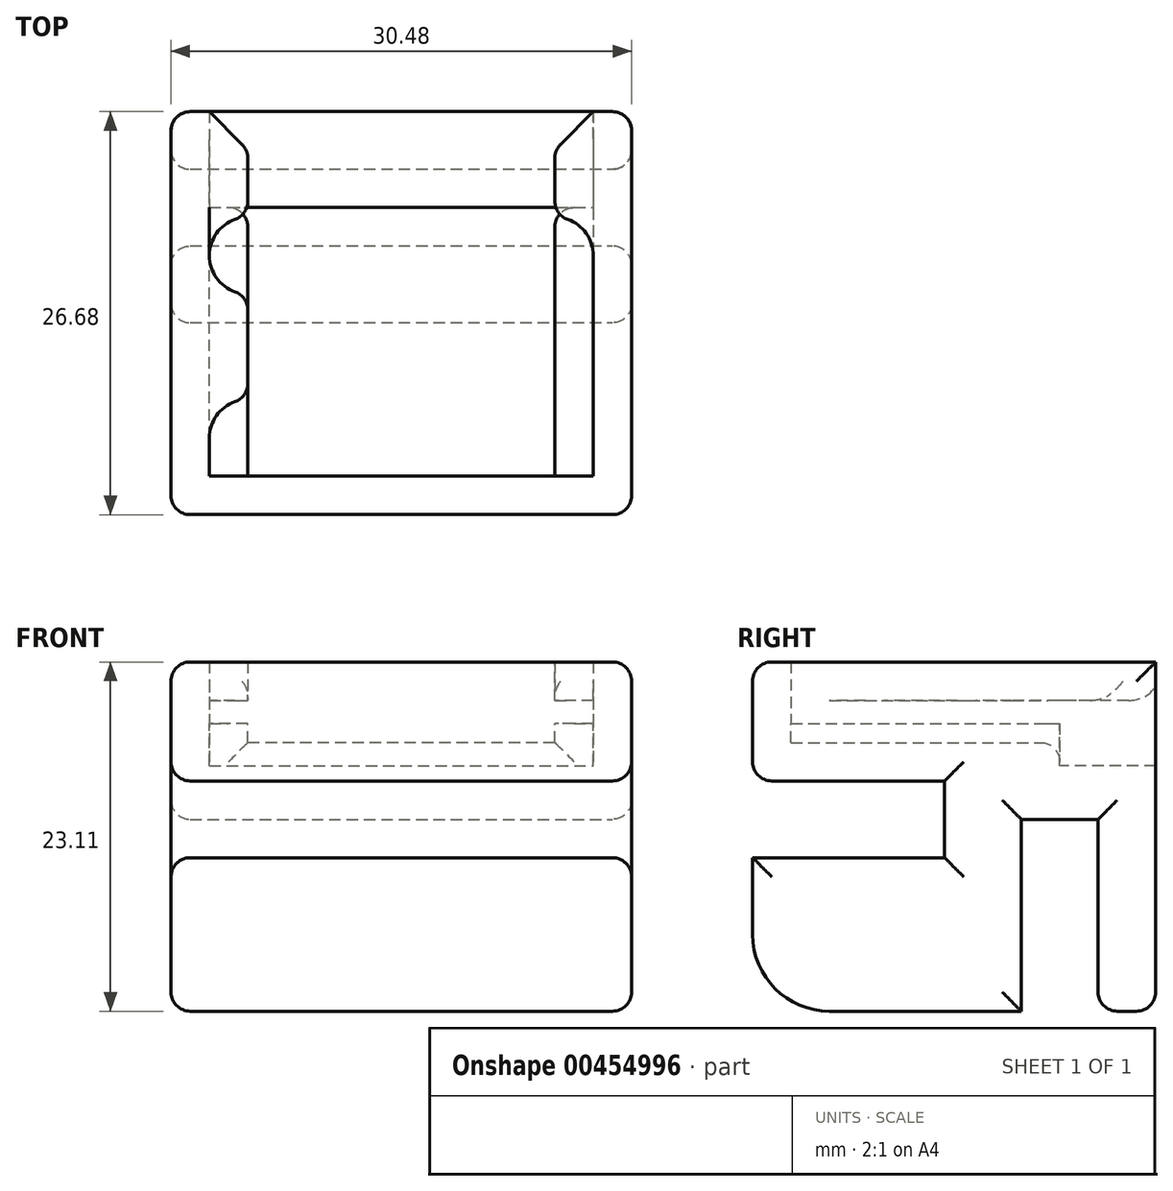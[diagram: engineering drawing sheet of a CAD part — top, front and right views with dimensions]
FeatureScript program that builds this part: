
annotation { "Feature Type Name" : "Feature", "Feature Type Description" : "" }
export const myFeature = defineFeature(function(context is Context, id is Id, definition is map)
    precondition{}
    {
        {
            var Q0;
            Q0=qCreatedBy(makeId("Top.planeOp"),FACE);
            var sketch = newSketch(context, id + "F0", { "sketchPlane" : qUnion([Q0])});
            skLineSegment(sketch, "E0.bottom", {"start": v(15.24, 13.33) * mm, "end": v(-15.24, 13.33) * mm});
            skLineSegment(sketch, "E0.top", {"start": v(15.24, -13.34) * mm, "end": v(-15.24, -13.34) * mm});
            skLineSegment(sketch, "E0.left", {"start": v(15.24, 13.33) * mm, "end": v(15.24, -13.34) * mm});
            skLineSegment(sketch, "E0.right", {"start": v(-15.24, 13.34) * mm, "end": v(-15.24, -13.33) * mm});
            skPoint(sketch, "E0.middle", {"position": v(0, 0) * mm});
            skSolve(sketch);
        }
        {
            var Q0;
            Q0 = qSketchRegion(id + "F0", true);
            extrude(context, id + "F1", {"entities" : qUnion([Q0]), "depth" : 19.05 * mm});
        }
        {
            var Q0;
            Q0=makeQuery(id+"F1.opExtrude","CAP_FACE",FACE,{"disambiguationData":[OSD([sQuery(id+"F0.wireOp",EDGE,"E0.bottom"),sQuery(id+"F0.wireOp",EDGE,"E0.top"),sQuery(id+"F0.wireOp",EDGE,"E0.left"),sQuery(id+"F0.wireOp",EDGE,"E0.right")])],"isStart":false});
            var sketch = newSketch(context, id + "F2", { "sketchPlane" : qUnion([Q0])});
            skLineSegment(sketch, "E1", {"start": v(-15.24, 13.33) * mm, "end": v(-15.24, -13.33) * mm});
            skLineSegment(sketch, "E2", {"start": v(-15.24, -13.33) * mm, "end": v(15.24, -13.34) * mm});
            skLineSegment(sketch, "E3", {"start": v(15.24, -13.34) * mm, "end": v(15.24, 13.33) * mm});
            skLineSegment(sketch, "E4", {"start": v(15.24, 13.33) * mm, "end": v(12.7, 13.33) * mm});
            skLineSegment(sketch, "E5", {"start": v(12.7, 13.33) * mm, "end": v(12.7, -10.8) * mm});
            skLineSegment(sketch, "E6", {"start": v(12.7, -10.8) * mm, "end": v(-12.7, -10.8) * mm});
            skLineSegment(sketch, "E7", {"start": v(-12.7, -10.8) * mm, "end": v(-12.7, 13.33) * mm});
            skLineSegment(sketch, "E8", {"start": v(-12.7, 13.33) * mm, "end": v(-15.24, 13.33) * mm});
            skLineSegment(sketch, "E9", {"start": v(-12.7, -10.8) * mm, "end": v(-12.7, -13.34) * mm, "construction": true});
            skSolve(sketch);
        }
        {
            var Q0;
            Q0 = qSketchRegion(id + "F2", true);
            extrude(context, id + "F3", {"entities" : qUnion([Q0]), "operationType" : NewBodyOperationType.ADD, "depth" : 1.52 * mm});
        }
        {
            var Q0;
            Q0=makeQuery(id+"F3.opExtrude","CAP_FACE",FACE,{"disambiguationData":[OSD([sQuery(id+"F2.wireOp",EDGE,"E1"),sQuery(id+"F2.wireOp",EDGE,"E2"),sQuery(id+"F2.wireOp",EDGE,"E3"),sQuery(id+"F2.wireOp",EDGE,"E4"),sQuery(id+"F2.wireOp",EDGE,"E5"),sQuery(id+"F2.wireOp",EDGE,"E6"),sQuery(id+"F2.wireOp",EDGE,"E7"),sQuery(id+"F2.wireOp",EDGE,"E8")])],"isStart":false});
            var sketch = newSketch(context, id + "F4", { "sketchPlane" : qUnion([Q0])});
            skLineSegment(sketch, "E10.0", {"start": v(15.24, 13.33) * mm, "end": v(12.7, 13.33) * mm});
            skLineSegment(sketch, "E10.1", {"start": v(15.24, 13.33) * mm, "end": v(15.24, -13.34) * mm});
            skLineSegment(sketch, "E10.2", {"start": v(15.24, -13.34) * mm, "end": v(-15.24, -13.34) * mm});
            skLineSegment(sketch, "E10.3", {"start": v(-15.24, 13.33) * mm, "end": v(-15.24, -13.33) * mm});
            skLineSegment(sketch, "E11.0", {"start": v(-12.7, 13.33) * mm, "end": v(-15.24, 13.33) * mm});
            skLineSegment(sketch, "E12", {"start": v(-12.7, 13.33) * mm, "end": v(-10.16, 10.8) * mm});
            skLineSegment(sketch, "E13", {"start": v(-10.16, 10.8) * mm, "end": v(-10.16, -5.71) * mm});
            skLineSegment(sketch, "E14", {"start": v(-12.7, -10.8) * mm, "end": v(0, -10.8) * mm});
            skLineSegment(sketch, "E15", {"start": v(0, -10.8) * mm, "end": v(0, 0) * mm, "construction": true});
            skArc(sketch, "E16", {"start": v(-10.16, -5.71) * mm, "mid": v(-11.96, -6.46) * mm, "end": v(-12.7, -8.25) * mm});
            skLineSegment(sketch, "E17", {"start": v(-10.16, -5.71) * mm, "end": v(-10.16, -8.25) * mm, "construction": true});
            skLineSegment(sketch, "E18", {"start": v(-12.7, -10.8) * mm, "end": v(-12.7, -8.25) * mm});
            skArc(sketch, "E19", {"start": v(-10.16, 6.35) * mm, "mid": v(-12.7, 3.81) * mm, "end": v(-10.16, 1.27) * mm});
            skLineSegment(sketch, "E20.MirrorCS", {"start": v(12.7, -10.8) * mm, "end": v(0, -10.8) * mm});
            skLineSegment(sketch, "E21.MirrorCS", {"start": v(10.16, -5.71) * mm, "end": v(10.16, -8.25) * mm, "construction": true});
            skArc(sketch, "E22.MirrorCS", {"start": v(10.16, -5.71) * mm, "mid": v(11.96, -6.46) * mm, "end": v(12.7, -8.25) * mm});
            skLineSegment(sketch, "E23.MirrorCS", {"start": v(12.7, 13.34) * mm, "end": v(10.16, 10.8) * mm});
            skLineSegment(sketch, "E24.MirrorCS", {"start": v(12.7, -10.8) * mm, "end": v(12.7, -8.25) * mm});
            skArc(sketch, "E25.MirrorCS", {"start": v(10.16, 6.35) * mm, "mid": v(12.7, 3.81) * mm, "end": v(10.16, 1.27) * mm});
            skLineSegment(sketch, "E26.MirrorCS", {"start": v(10.16, 10.8) * mm, "end": v(10.16, -5.71) * mm});
            skSolve(sketch);
        }
        {
            var Q0;
            {var subQ0=sQuery(id+"F4.wireOp",EDGE,"E16");Q0=makeQuery(id+"F4.imprint","IMPRINT",FACE,{"disambiguationData":[TD([[makeQuery(id+"F4.imprint","IMPRINT",EDGE,{"derivedFrom":subQ0}),-1.0]])]});}
            var Q1;
            {var subQ0=sQuery(id+"F4.wireOp",EDGE,"E12");Q1=makeQuery(id+"F4.imprint","IMPRINT",FACE,{"disambiguationData":[TD([[makeQuery(id+"F4.imprint","IMPRINT",EDGE,{"derivedFrom":subQ0}),-1.0]])]});}
            var Q2;
            {var subQ3=sQuery(id+"F4.wireOp",EDGE,"E10.0");Q2=makeQuery(id+"F4.imprint","IMPRINT",FACE,{"disambiguationData":[TD([[makeQuery(id+"F4.imprint","IMPRINT",EDGE,{"derivedFrom":subQ3}),1.0]])]});}
            var Q3;
            {var subQ0=sQuery(id+"F4.wireOp",EDGE,"E22.MirrorCS");Q3=makeQuery(id+"F4.imprint","IMPRINT",FACE,{"disambiguationData":[TD([[makeQuery(id+"F4.imprint","IMPRINT",EDGE,{"derivedFrom":subQ0}),1.0]])]});}
            var Q4;
            {var subQ0=sQuery(id+"F4.wireOp",EDGE,"E23.MirrorCS");Q4=makeQuery(id+"F4.imprint","IMPRINT",FACE,{"disambiguationData":[TD([[makeQuery(id+"F4.imprint","IMPRINT",EDGE,{"derivedFrom":subQ0}),1.0]])]});}
            extrude(context, id + "F5", {"entities" : qUnion([Q0, Q1, Q2, Q3, Q4]), "operationType" : NewBodyOperationType.ADD, "depth" : 2.54 * mm});
        }
        {
            var Q0;
            Q0=makeQuery(id+"F1.opExtrude","CAP_FACE",FACE,{"disambiguationData":[OSD([sQuery(id+"F0.wireOp",EDGE,"E0.bottom"),sQuery(id+"F0.wireOp",EDGE,"E0.top"),sQuery(id+"F0.wireOp",EDGE,"E0.left"),sQuery(id+"F0.wireOp",EDGE,"E0.right")])],"isStart":false});
            var sketch = newSketch(context, id + "F6", { "sketchPlane" : qUnion([Q0])});
            skLineSegment(sketch, "E27.bottom", {"start": v(-10.16, -10.8) * mm, "end": v(10.16, -10.8) * mm});
            skLineSegment(sketch, "E27.top", {"start": v(-10.16, 13.33) * mm, "end": v(10.16, 13.33) * mm});
            skLineSegment(sketch, "E27.left", {"start": v(-10.16, -10.8) * mm, "end": v(-10.16, 13.33) * mm});
            skLineSegment(sketch, "E27.right", {"start": v(10.16, -10.8) * mm, "end": v(10.16, 13.33) * mm});
            skPoint(sketch, "E27.middle", {"position": v(0, 1.27) * mm});
            skSolve(sketch);
        }
        {
            var Q0;
            Q0 = qSketchRegion(id + "F6", true);
            extrude(context, id + "F7", {"entities" : qUnion([Q0]), "operationType" : NewBodyOperationType.REMOVE, "oppositeDirection" : true, "depth" : 1.27 * mm});
        }
        {
            var Q0;
            {var subQ0=sQuery(id+"F0.wireOp",EDGE,"E0.bottom");Q0=makeQuery(id+"F7.boolean.opBoolean","SPLIT",FACE,{"disambiguationData":[TD([makeQuery(id+"F3.opExtrude","SWEPT_FACE",FACE,{"disambiguationData":[OSD([sQuery(id+"F2.wireOp",EDGE,"E5")])]})])],"derivedFrom":makeQuery(id+"F1.opExtrude","CAP_FACE",FACE,{"disambiguationData":[OSD([subQ0,sQuery(id+"F0.wireOp",EDGE,"E0.top"),sQuery(id+"F0.wireOp",EDGE,"E0.left"),sQuery(id+"F0.wireOp",EDGE,"E0.right")])],"isStart":false})});}
            var sketch = newSketch(context, id + "F8", { "sketchPlane" : qUnion([Q0])});
            skLineSegment(sketch, "E28.bottom", {"start": v(-12.7, 13.33) * mm, "end": v(12.7, 13.33) * mm});
            skLineSegment(sketch, "E28.top", {"start": v(-12.7, 6.98) * mm, "end": v(12.7, 6.98) * mm});
            skLineSegment(sketch, "E28.left", {"start": v(-12.7, 13.33) * mm, "end": v(-12.7, 6.98) * mm});
            skLineSegment(sketch, "E28.right", {"start": v(12.7, 13.33) * mm, "end": v(12.7, 6.98) * mm});
            skSolve(sketch);
        }
        {
            var Q0;
            Q0 = qSketchRegion(id + "F8", true);
            extrude(context, id + "F9", {"entities" : qUnion([Q0]), "operationType" : NewBodyOperationType.REMOVE, "oppositeDirection" : true, "depth" : 2.8 * mm});
        }
        {
            var Q0;
            Q0=makeQuery(id+"F5.boolean.opBoolean","MERGE",FACE,{"derivedFrom":[makeQuery(id+"F3.boolean.opBoolean","MERGE",FACE,{"derivedFrom":[makeQuery(id+"F1.opExtrude","SWEPT_FACE",FACE,{"disambiguationData":[OSD([sQuery(id+"F0.wireOp",EDGE,"E0.left")])]}),makeQuery(id+"F3.opExtrude","SWEPT_FACE",FACE,{"disambiguationData":[OSD([sQuery(id+"F2.wireOp",EDGE,"E3")])]})]}),makeQuery(id+"F5.opExtrude","SWEPT_FACE",FACE,{"disambiguationData":[OSD([sQuery(id+"F4.wireOp",EDGE,"E10.1")])]})]});
            var sketch = newSketch(context, id + "F10", { "sketchPlane" : qUnion([Q0])});
            skLineSegment(sketch, "E29.bottom", {"start": v(-13.34, 15.24) * mm, "end": v(-0.64, 15.24) * mm});
            skLineSegment(sketch, "E29.top", {"start": v(-13.34, 10.16) * mm, "end": v(-0.64, 10.16) * mm});
            skLineSegment(sketch, "E29.left", {"start": v(-13.34, 15.24) * mm, "end": v(-13.34, 10.16) * mm});
            skLineSegment(sketch, "E29.right", {"start": v(-0.64, 15.24) * mm, "end": v(-0.63, 10.16) * mm});
            skLineSegment(sketch, "E30.bottom", {"start": v(4.44, 0) * mm, "end": v(9.52, 0) * mm});
            skLineSegment(sketch, "E30.top", {"start": v(4.44, 12.7) * mm, "end": v(9.52, 12.7) * mm});
            skLineSegment(sketch, "E30.left", {"start": v(4.44, 0) * mm, "end": v(4.44, 12.7) * mm});
            skLineSegment(sketch, "E30.right", {"start": v(9.53, 0) * mm, "end": v(9.53, 12.7) * mm});
            skSolve(sketch);
        }
        {
            var Q0;
            Q0 = qSketchRegion(id + "F10", true);
            extrude(context, id + "F11", {"entities" : qUnion([Q0]), "operationType" : NewBodyOperationType.REMOVE, "endBound" : BoundingType.THROUGH_ALL, "oppositeDirection" : true, "depth" : 25.4 * mm});
        }
        {
            var Q0;
            Q0=makeQuery(id+"F1.opExtrude","CAP_EDGE",EDGE,{"disambiguationData":[OSD([sQuery(id+"F0.wireOp",EDGE,"E0.top")])],"isStart":true});
            fillet(context, id + "F12", {"entities" : qUnion([Q0]), "radius" : 5.08 * mm, "tangentPropagation" : true, "allowEdgeOverflow" : false});
        }
        {
            var Q0;
            Q0=makeQuery(id+"F11.boolean.opBoolean","COPY",EDGE,{"derivedFrom":makeQuery(id+"F11.opExtrude","SWEPT_EDGE",EDGE,{"disambiguationData":[OSD([sQuery(id+"F0.wireOp",EDGE,"E0.top"),sQuery(id+"F0.wireOp",EDGE,"E0.left"),sQuery(id+"F2.wireOp",EDGE,"E2"),sQuery(id+"F2.wireOp",EDGE,"E3"),sQuery(id+"F4.wireOp",EDGE,"E10.1"),sQuery(id+"F4.wireOp",EDGE,"E10.2"),sQuery(id+"F10.wireOp",EDGE,"E29.top"),sQuery(id+"F10.wireOp",EDGE,"E29.left")])]})});
            var Q1;
            Q1=makeQuery(id+"F11.boolean.opBoolean","COPY",EDGE,{"derivedFrom":makeQuery(id+"F11.opExtrude","SWEPT_EDGE",EDGE,{"disambiguationData":[OSD([sQuery(id+"F0.wireOp",EDGE,"E0.top"),sQuery(id+"F0.wireOp",EDGE,"E0.left"),sQuery(id+"F2.wireOp",EDGE,"E2"),sQuery(id+"F2.wireOp",EDGE,"E3"),sQuery(id+"F4.wireOp",EDGE,"E10.1"),sQuery(id+"F4.wireOp",EDGE,"E10.2"),sQuery(id+"F10.wireOp",EDGE,"E29.bottom"),sQuery(id+"F10.wireOp",EDGE,"E29.left")])]})});
            var Q2;
            Q2=makeQuery(id+"F11.boolean.opBoolean","COPY",EDGE,{"derivedFrom":makeQuery(id+"F11.opExtrude","SWEPT_EDGE",EDGE,{"disambiguationData":[OSD([sQuery(id+"F0.wireOp",EDGE,"E0.left"),sQuery(id+"F10.wireOp",EDGE,"E30.bottom"),sQuery(id+"F10.wireOp",EDGE,"E30.left")])]})});
            var Q3;
            Q3=makeQuery(id+"F11.boolean.opBoolean","COPY",EDGE,{"derivedFrom":makeQuery(id+"F11.opExtrude","SWEPT_EDGE",EDGE,{"disambiguationData":[OSD([sQuery(id+"F0.wireOp",EDGE,"E0.left"),sQuery(id+"F10.wireOp",EDGE,"E30.bottom"),sQuery(id+"F10.wireOp",EDGE,"E30.right")])]})});
            var Q4;
            Q4=makeQuery(id+"F5.boolean.opBoolean","MERGE",FACE,{"derivedFrom":[makeQuery(id+"F3.boolean.opBoolean","MERGE",FACE,{"derivedFrom":[makeQuery(id+"F1.opExtrude","SWEPT_FACE",FACE,{"disambiguationData":[OSD([sQuery(id+"F0.wireOp",EDGE,"E0.left")])]}),makeQuery(id+"F3.opExtrude","SWEPT_FACE",FACE,{"disambiguationData":[OSD([sQuery(id+"F2.wireOp",EDGE,"E3")])]})]}),makeQuery(id+"F5.opExtrude","SWEPT_FACE",FACE,{"disambiguationData":[OSD([sQuery(id+"F4.wireOp",EDGE,"E10.1")])]})]});
            var Q5;
            Q5=makeQuery(id+"F5.boolean.opBoolean","MERGE",FACE,{"derivedFrom":[makeQuery(id+"F3.boolean.opBoolean","MERGE",FACE,{"derivedFrom":[makeQuery(id+"F1.opExtrude","SWEPT_FACE",FACE,{"disambiguationData":[OSD([sQuery(id+"F0.wireOp",EDGE,"E0.right")])]}),makeQuery(id+"F3.opExtrude","SWEPT_FACE",FACE,{"disambiguationData":[OSD([sQuery(id+"F2.wireOp",EDGE,"E1")])]})]}),makeQuery(id+"F5.opExtrude","SWEPT_FACE",FACE,{"disambiguationData":[OSD([sQuery(id+"F4.wireOp",EDGE,"E10.3")])]})]});
            var Q6;
            Q6=makeQuery(id+"F9.boolean.opBoolean","COPY",EDGE,{"derivedFrom":makeQuery(id+"F9.opExtrude","CAP_EDGE",EDGE,{"disambiguationData":[OSD([sQuery(id+"F8.wireOp",EDGE,"E28.bottom")])],"isStart":false})});
            var Q7;
            Q7=makeQuery(id+"F9.boolean.opBoolean","INTERSECT",EDGE,{"derivedFrom":[makeQuery(id+"F7.boolean.opBoolean","COPY",FACE,{"derivedFrom":makeQuery(id+"F7.opExtrude","CAP_FACE",FACE,{"disambiguationData":[OSD([sQuery(id+"F6.wireOp",EDGE,"E27.bottom"),sQuery(id+"F6.wireOp",EDGE,"E27.top"),sQuery(id+"F6.wireOp",EDGE,"E27.left"),sQuery(id+"F6.wireOp",EDGE,"E27.right")])],"isStart":false})}),makeQuery(id+"F9.opExtrude","SWEPT_FACE",FACE,{"disambiguationData":[OSD([sQuery(id+"F8.wireOp",EDGE,"E28.top")])]})]});
            var Q8;
            {var subQ0=sQuery(id+"F8.wireOp",EDGE,"E28.top");Q8=makeQuery(id+"F9.boolean.opBoolean","COPY",EDGE,{"disambiguationData":[TD([makeQuery(id+"F3.opExtrude","SWEPT_FACE",FACE,{"disambiguationData":[OSD([sQuery(id+"F2.wireOp",EDGE,"E5")])]})])],"derivedFrom":makeQuery(id+"F9.opExtrude","CAP_EDGE",EDGE,{"disambiguationData":[OSD([subQ0])],"isStart":true})});}
            var Q9;
            Q9=makeQuery(id+"F9.boolean.opBoolean","INTERSECT",EDGE,{"derivedFrom":[makeQuery(id+"F7.boolean.opBoolean","COPY",FACE,{"derivedFrom":makeQuery(id+"F7.opExtrude","SWEPT_FACE",FACE,{"disambiguationData":[OSD([sQuery(id+"F6.wireOp",EDGE,"E27.right")])]})}),makeQuery(id+"F9.opExtrude","SWEPT_FACE",FACE,{"disambiguationData":[OSD([sQuery(id+"F8.wireOp",EDGE,"E28.top")])]})]});
            var Q10;
            Q10=makeQuery(id+"F9.boolean.opBoolean","INTERSECT",EDGE,{"derivedFrom":[makeQuery(id+"F7.boolean.opBoolean","COPY",FACE,{"derivedFrom":makeQuery(id+"F7.opExtrude","SWEPT_FACE",FACE,{"disambiguationData":[OSD([sQuery(id+"F6.wireOp",EDGE,"E27.left")])]})}),makeQuery(id+"F9.opExtrude","SWEPT_FACE",FACE,{"disambiguationData":[OSD([sQuery(id+"F8.wireOp",EDGE,"E28.top")])]})]});
            var Q11;
            {var subQ0=sQuery(id+"F8.wireOp",EDGE,"E28.top");Q11=makeQuery(id+"F9.boolean.opBoolean","COPY",EDGE,{"disambiguationData":[TD([makeQuery(id+"F3.opExtrude","SWEPT_FACE",FACE,{"disambiguationData":[OSD([sQuery(id+"F2.wireOp",EDGE,"E7")])]})])],"derivedFrom":makeQuery(id+"F9.opExtrude","CAP_EDGE",EDGE,{"disambiguationData":[OSD([subQ0])],"isStart":true})});}
            var Q12;
            Q12=makeQuery(id+"F5.opExtrude","CAP_EDGE",EDGE,{"disambiguationData":[OSD([sQuery(id+"F4.wireOp",EDGE,"E12")])],"isStart":true});
            var Q13;
            Q13=makeQuery(id+"F5.opExtrude","CAP_EDGE",EDGE,{"disambiguationData":[OSD([sQuery(id+"F4.wireOp",EDGE,"E23.MirrorCS")])],"isStart":true});
            var Q14;
            Q14=makeQuery(id+"F5.opExtrude","SWEPT_EDGE",EDGE,{"disambiguationData":[OSD([sQuery(id+"F4.wireOp",EDGE,"E12"),sQuery(id+"F4.wireOp",EDGE,"E13")])]});
            var Q15;
            Q15=makeQuery(id+"F5.opExtrude","SWEPT_EDGE",EDGE,{"disambiguationData":[OSD([sQuery(id+"F4.wireOp",EDGE,"E23.MirrorCS"),sQuery(id+"F4.wireOp",EDGE,"E26.MirrorCS")])]});
            var Q16;
            {var subQ0=sQuery(id+"F4.wireOp",EDGE,"E19");var subQ1=sQuery(id+"F4.wireOp",EDGE,"E13");Q16=makeQuery(id+"F5.opExtrude","SWEPT_EDGE",EDGE,{"disambiguationData":[OSD([subQ1,subQ0]),TDD([makeQuery(id+"F4.imprint","INTERSECT",VERTEX,{"disambiguationData":[OD(0.0)],"derivedFrom":[subQ1,subQ0]})])]});}
            var Q17;
            {var subQ0=sQuery(id+"F4.wireOp",EDGE,"E19");var subQ1=sQuery(id+"F4.wireOp",EDGE,"E13");Q17=makeQuery(id+"F5.opExtrude","SWEPT_EDGE",EDGE,{"disambiguationData":[OSD([subQ1,subQ0]),TDD([makeQuery(id+"F4.imprint","INTERSECT",VERTEX,{"disambiguationData":[OD(1.0)],"derivedFrom":[subQ1,subQ0]})])]});}
            var Q18;
            {var subQ0=sQuery(id+"F4.wireOp",EDGE,"E26.MirrorCS");var subQ1=sQuery(id+"F4.wireOp",EDGE,"E25.MirrorCS");Q18=makeQuery(id+"F5.opExtrude","SWEPT_EDGE",EDGE,{"disambiguationData":[OSD([subQ1,subQ0]),TDD([makeQuery(id+"F4.imprint","INTERSECT",VERTEX,{"disambiguationData":[OD(0.0)],"derivedFrom":[subQ1,subQ0]})])]});}
            var Q19;
            {var subQ0=sQuery(id+"F4.wireOp",EDGE,"E26.MirrorCS");var subQ1=sQuery(id+"F4.wireOp",EDGE,"E25.MirrorCS");Q19=makeQuery(id+"F5.opExtrude","SWEPT_EDGE",EDGE,{"disambiguationData":[OSD([subQ1,subQ0]),TDD([makeQuery(id+"F4.imprint","INTERSECT",VERTEX,{"disambiguationData":[OD(1.0)],"derivedFrom":[subQ1,subQ0]})])]});}
            var Q20;
            Q20=makeQuery(id+"F5.opExtrude","SWEPT_EDGE",EDGE,{"disambiguationData":[OSD([sQuery(id+"F4.wireOp",EDGE,"E22.MirrorCS"),sQuery(id+"F4.wireOp",EDGE,"E26.MirrorCS")])]});
            var Q21;
            Q21=makeQuery(id+"F5.opExtrude","SWEPT_EDGE",EDGE,{"disambiguationData":[OSD([sQuery(id+"F4.wireOp",EDGE,"E13"),sQuery(id+"F4.wireOp",EDGE,"E16")])]});
            var Q22;
            Q22=makeQuery(id+"F1.opExtrude","CAP_EDGE",EDGE,{"disambiguationData":[OSD([sQuery(id+"F0.wireOp",EDGE,"E0.bottom")])],"isStart":true});
            var Q23;
            Q23=makeQuery(id+"F5.opExtrude","CAP_EDGE",EDGE,{"disambiguationData":[OSD([sQuery(id+"F4.wireOp",EDGE,"E10.2")])],"isStart":false});
            fillet(context, id + "F13", {"entities" : qUnion([Q0, Q1, Q2, Q3, Q4, Q5, Q6, Q7, Q8, Q9, Q10, Q11, Q12, Q13, Q14, Q15, Q16, Q17, Q18, Q19, Q20, Q21, Q22, Q23]), "radius" : 1.27 * mm, "tangentPropagation" : true, "allowEdgeOverflow" : false});
        }
    });
